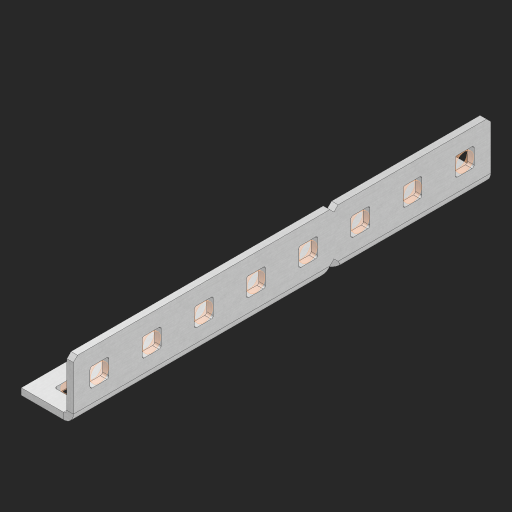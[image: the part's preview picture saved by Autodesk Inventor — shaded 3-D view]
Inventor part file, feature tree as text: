
AUTODESK INVENTOR PART (.ipt)
format: ipt  version: 2023 (Build 270158000, 158)  size: 543,744 bytes
history: native  units: in
note: dims shown in document units (in); Inventor stores cm internally (conversion verified against a paired STEP export)
features: other x21, extrude x15, sheet_metal_op x10, sketch x8, mirror x1, pattern_linear x1, chamfer x1
ambient origin geometry x8: Origin, YZ Plane, XZ Plane, XY Plane, X Axis, Y Axis, Z Axis, Center Point
bodies: Solid1 (feature_tree), Body (feature_tree)
feature tree (57):
  other  "Flange Pattern Plane"
  sheet_metal_op  "Flange Pattern"
  sheet_metal_op  "Body Pattern"
  other  "Arc Length"
  mirror  "Notch Mirror"
  pattern_linear  "Notch Pattern"  Spacing1=0.25in  [1 undecoded]
  chamfer  "End Chamfer"
  extrude  "Half Cut"  Depth=0.0625in
  sketch  "Sketch1"  dims[d0=1.5in]
  other  "Plate1"
  sketch  "Sketch2"  dims[d1=4.0in]
  other  "Plate2"
  sheet_metal_op  "Bend1"
  sheet_metal_op  "Corner1"
  sketch  "Sketch3"  dims[d2=0.0625in]
  other  "Flange Pattern Sketch"
  sketch  "Sketch7"  dims[d3=0.0625in]
  other  "Srf1"
  other  "Srf2"
  sketch  "Sketch8"  dims[d4=0.0312in]
  sketch  "Sketch9"  dims[d5=0.125in]
  other  "Srf91"
  sheet_metal_op  "Body Pattern Sketch"
  other  "Srf92"
  sketch  "Sketch13"  dims[d6=0.0625in]
  sketch  "Sketch14"  dims[d7=0.5in d8=90.0deg d9=0.0312in d10=0.25in d11=0.0625in d12=0.0625in d16=0.182in d17=0.02in d18=0.0625in d19=0.0in d20=0.25in d21=0.25in d46=0.172in d47=1.0in d48=0.0in d49=0.182in d50=0.02in d51=0.25in d52=0.25in d53=0.0625in d54=0.0in d55=0.172in d56=1.0in d57=0.0in d60=3.1496in d62=0.5in d63=0.3937in d65=0.5in d85=0.1473in d86=0.1782in d88=0.04in d89=0.0625in d90=0.0in d91=0.04in d92=0.0491in d95=2.5in d96=0.04in d97=0.25in d98=45.0deg d101=0.0in d102=2.497in d131=0.5in d132=3.1496in d134=0.5in d139=0.5in]
  other  "Srf856"
  other  "Srf1310"
  other  "Srf1311"
  other  "Srf1312"
  other  "Srf1376"
  other  "Srf1377"
  other  "Srf1728"
  other  "Srf1755"
  other  "Srf1878"
  other  "Srf1879"
  other  "Srf1942"
  other  "Srf1943"
  sheet_metal_op  "Flange Stamp"
  sheet_metal_op  "Flange Circle"
  sheet_metal_op  "Body Stamp"
  sheet_metal_op  "Body Circle"
  sheet_metal_op  "Notch"
  extrude  "ExtrusionSrf2"  Depth=0.0625in
  extrude  "ExtrusionSrf92"  Depth=0.5in
  extrude  "ExtrusionSrf856"  Depth=0.02in
  extrude  "ExtrusionSrf1310"  Depth=0.0625in
  extrude  "ExtrusionSrf1311"  TaperAngle=0.0deg  [1 undecoded]
  extrude  "ExtrusionSrf1312"  Depth=0.5in
  extrude  "ExtrusionSrf1376"  Depth=0.5in
  extrude  "ExtrusionSrf1377"  Depth=0.5in
  extrude  "ExtrusionSrf1728"  Depth=0.5in TaperAngle=0.0deg
  extrude  "ExtrusionSrf1755"  Depth=0.5in
  extrude  "ExtrusionSrf1878"  Depth=0.02in
  extrude  "ExtrusionSrf1879"  Depth=0.5in
  extrude  "ExtrusionSrf1942"  Depth=0.5in
  extrude  "ExtrusionSrf1943"  Depth=0.0625in
note: 2 required parameter values undecoded (feature->parameter linkage not recoverable at this tier; creation-order binding heuristic only, values carry confidence <= 0.55)
